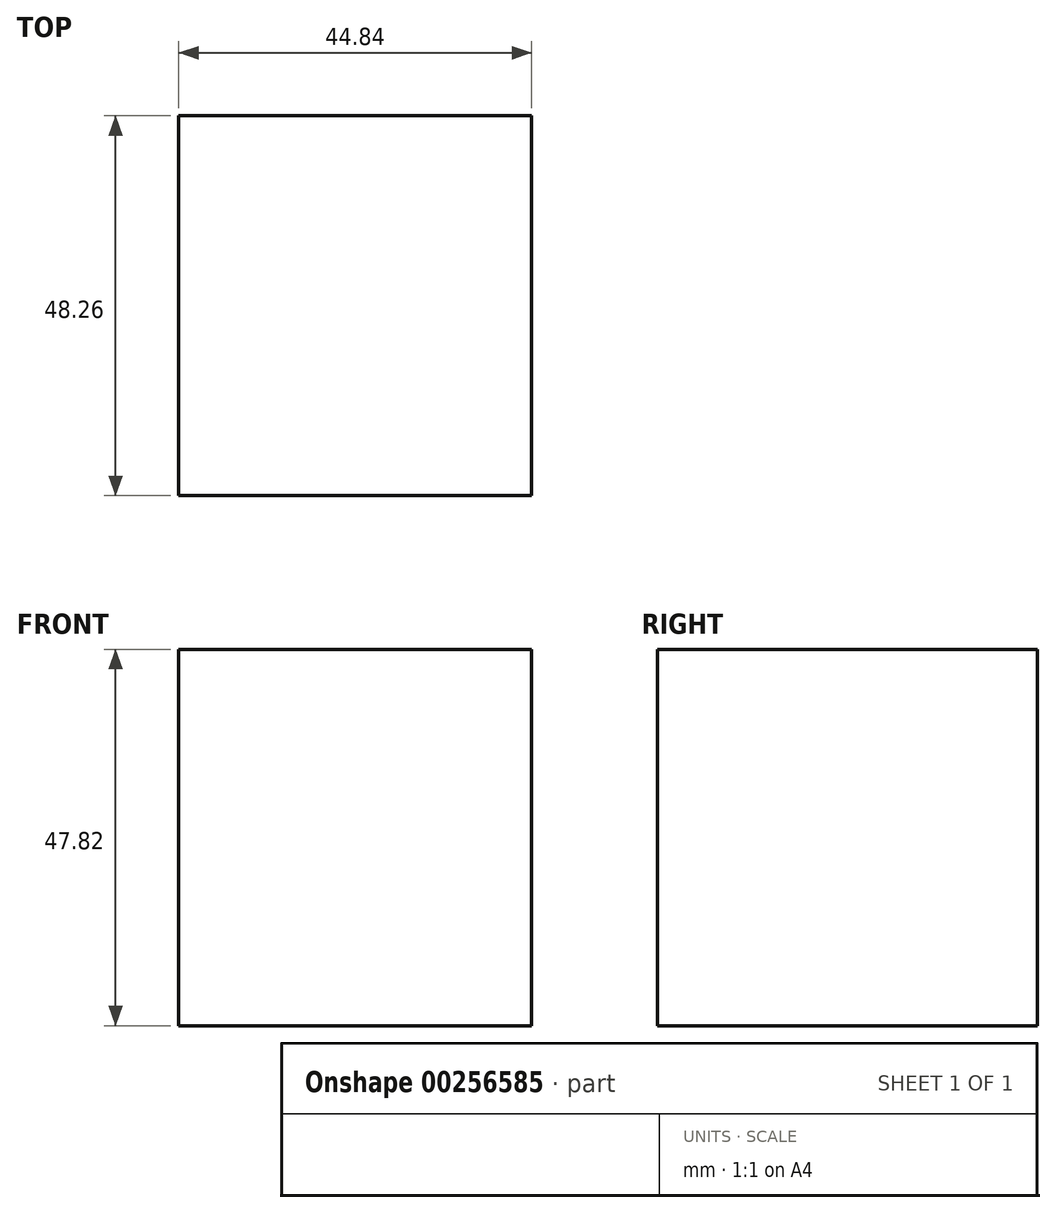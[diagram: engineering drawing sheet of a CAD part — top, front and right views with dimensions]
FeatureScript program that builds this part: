
annotation { "Feature Type Name" : "Feature", "Feature Type Description" : "" }
export const myFeature = defineFeature(function(context is Context, id is Id, definition is map)
    precondition{}
    {
        {
            var Q0;
            Q0=qCreatedBy(makeId("Front.planeOp"),FACE);
            var sketch = newSketch(context, id + "F0", { "sketchPlane" : qUnion([Q0])});
            skLineSegment(sketch, "E0.bottom", {"start": v(-26.4, 16.06) * mm, "end": v(18.44, 16.06) * mm});
            skLineSegment(sketch, "E0.top", {"start": v(-26.4, -31.76) * mm, "end": v(18.44, -31.76) * mm});
            skLineSegment(sketch, "E0.left", {"start": v(-26.4, 16.06) * mm, "end": v(-26.4, -31.76) * mm});
            skLineSegment(sketch, "E0.right", {"start": v(18.44, 16.06) * mm, "end": v(18.44, -31.76) * mm});
            skSolve(sketch);
        }
        {
            var Q0;
            Q0=makeQuery(id+"F0.imprint","IMPRINT",FACE,{"disambiguationData":[TD([[makeQuery(id+"F0.imprint","IMPRINT",EDGE,{"derivedFrom":sQuery(id+"F0.wireOp",EDGE,"E0.bottom")}),-1.0]])]});
            extrude(context, id + "F1", {"entities" : qUnion([Q0]), "depth" : 48.26 * mm});
        }
    });
